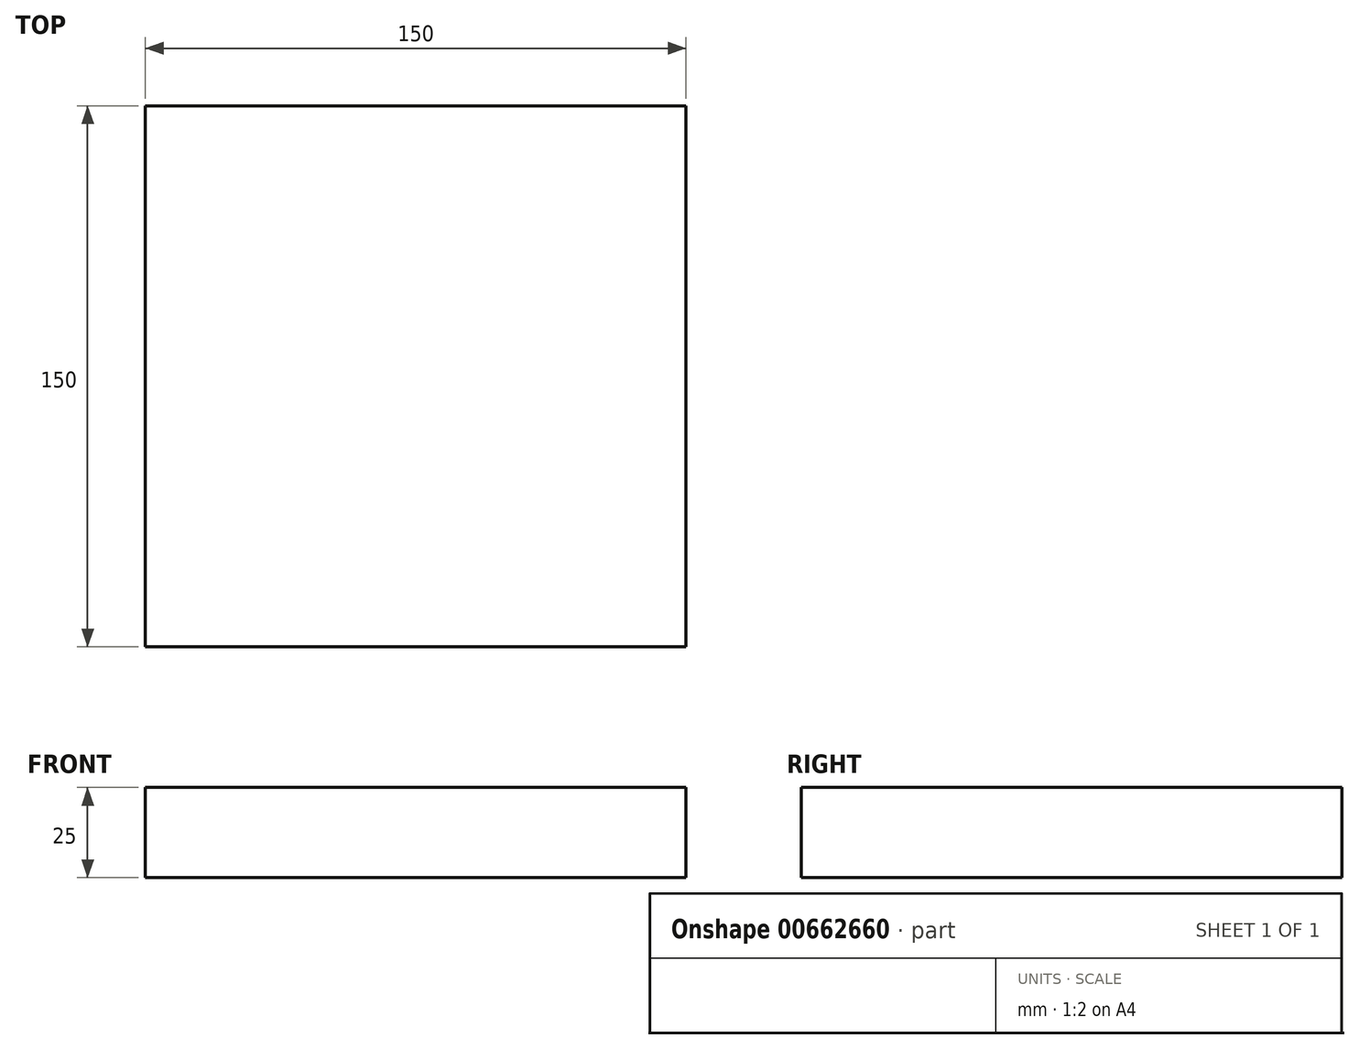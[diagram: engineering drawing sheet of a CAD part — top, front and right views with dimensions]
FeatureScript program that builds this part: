
annotation { "Feature Type Name" : "Feature", "Feature Type Description" : "" }
export const myFeature = defineFeature(function(context is Context, id is Id, definition is map)
    precondition{}
    {
        {
            var Q0;
            Q0=qCreatedBy(makeId("Top.planeOp"),FACE);
            var sketch = newSketch(context, id + "F0", { "sketchPlane" : qUnion([Q0])});
            skLineSegment(sketch, "E0.bottom", {"start": v(-75, 75) * mm, "end": v(75, 75) * mm});
            skLineSegment(sketch, "E0.top", {"start": v(-75, -75) * mm, "end": v(75, -75) * mm});
            skLineSegment(sketch, "E0.left", {"start": v(-75, 75) * mm, "end": v(-75, -75) * mm});
            skLineSegment(sketch, "E0.right", {"start": v(75, 75) * mm, "end": v(75, -75) * mm});
            skPoint(sketch, "E0.middle", {"position": v(0, 0) * mm});
            skSolve(sketch);
        }
        {
            var Q0;
            Q0=makeQuery(id+"F0.imprint","IMPRINT",FACE,{"disambiguationData":[TD([[makeQuery(id+"F0.imprint","IMPRINT",EDGE,{"derivedFrom":sQuery(id+"F0.wireOp",EDGE,"E0.bottom")}),-1.0]])]});
            extrude(context, id + "F1", {"entities" : qUnion([Q0]), "depth" : 25 * mm, "offsetDistance" : 25 * mm});
        }
    });
